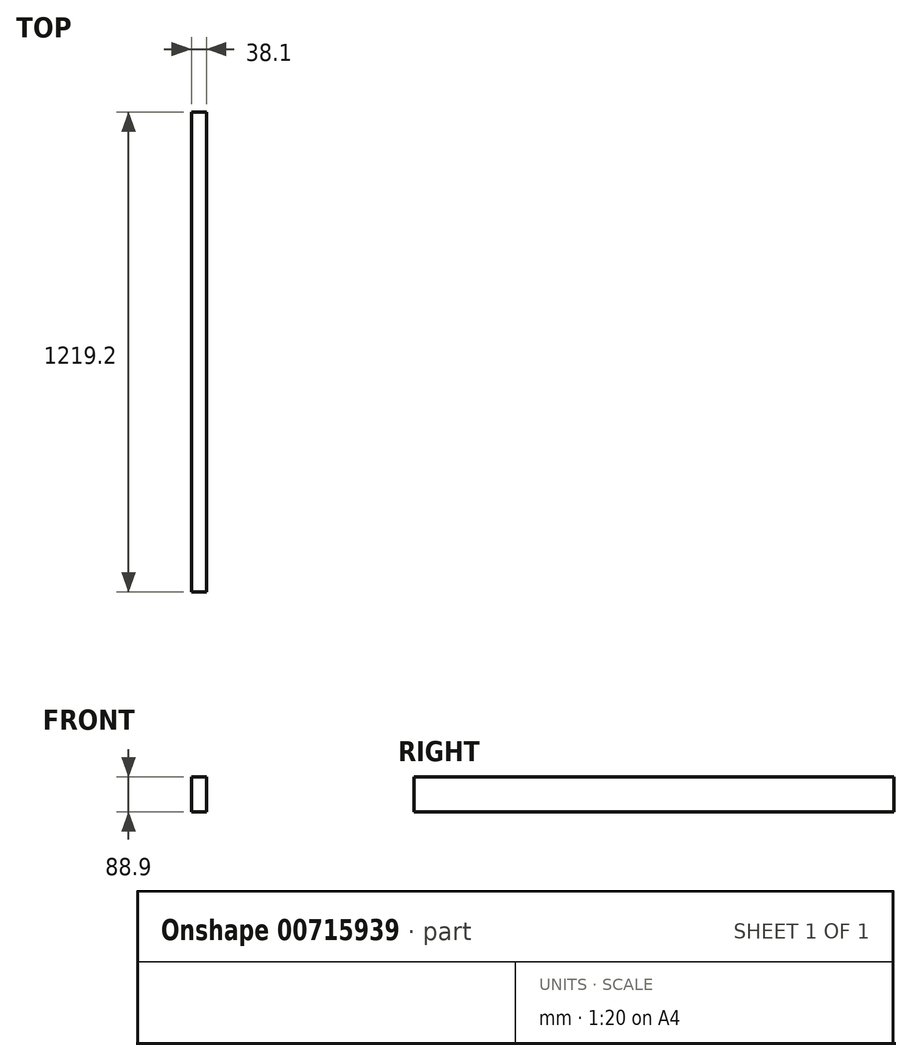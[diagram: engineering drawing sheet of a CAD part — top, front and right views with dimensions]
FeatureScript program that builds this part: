
annotation { "Feature Type Name" : "Feature", "Feature Type Description" : "" }
export const myFeature = defineFeature(function(context is Context, id is Id, definition is map)
    precondition{}
    {
        {
            var Q0;
            Q0=qCreatedBy(makeId("Front.planeOp"),FACE);
            var sketch = newSketch(context, id + "F0", { "sketchPlane" : qUnion([Q0])});
            skLineSegment(sketch, "E0.bottom", {"start": v(-19.05, 44.45) * mm, "end": v(19.05, 44.45) * mm});
            skLineSegment(sketch, "E0.top", {"start": v(-19.05, -44.45) * mm, "end": v(19.05, -44.45) * mm});
            skLineSegment(sketch, "E0.left", {"start": v(-19.05, 44.45) * mm, "end": v(-19.05, -44.45) * mm});
            skLineSegment(sketch, "E0.right", {"start": v(19.05, 44.45) * mm, "end": v(19.05, -44.45) * mm});
            skPoint(sketch, "E0.middle", {"position": v(0, 0) * mm});
            skSolve(sketch);
        }
        {
            var Q0;
            Q0=makeQuery(id+"F0.imprint","IMPRINT",FACE,{"disambiguationData":[TD([[makeQuery(id+"F0.imprint","IMPRINT",EDGE,{"derivedFrom":sQuery(id+"F0.wireOp",EDGE,"E0.bottom")}),-1.0]])]});
            extrude(context, id + "F1", {"entities" : qUnion([Q0]), "endBound" : BoundingType.SYMMETRIC, "depth" : 1219.2 * mm, "offsetDistance" : 25.4 * mm});
        }
    });
